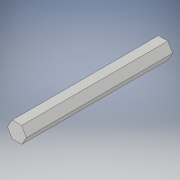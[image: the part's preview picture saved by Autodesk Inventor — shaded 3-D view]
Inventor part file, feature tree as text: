
AUTODESK INVENTOR PART (.ipt)
format: ipt  version: 2018 (Build 220112000, 112)  size: 94,208 bytes
history: native  units: in
note: dims shown in document units (in); Inventor stores cm internally (conversion verified against a paired STEP export)
features: extrude x1, sketch x1
ambient origin geometry x8: Origin, YZ Plane, XZ Plane, XY Plane, X Axis, Y Axis, Z Axis, Center Point
bodies: Solid1 (feature_tree)
feature tree (2):
  extrude  "Extrusion1"  Depth=4.458in TaperAngle=0.0deg
  sketch  "Sketch1"  dims[d0=0.5in d1=4.458in d2=0.0in]
